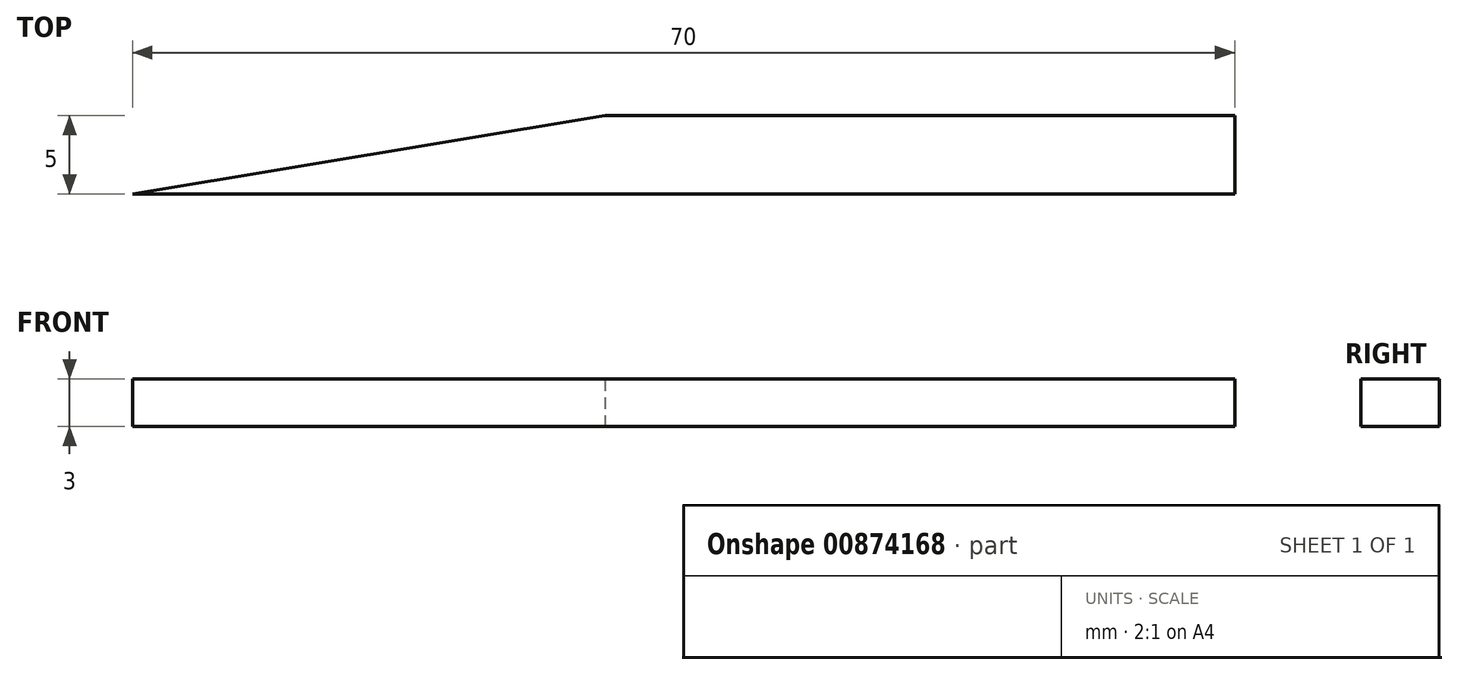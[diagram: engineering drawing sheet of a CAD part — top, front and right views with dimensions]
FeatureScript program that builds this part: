
annotation { "Feature Type Name" : "Feature", "Feature Type Description" : "" }
export const myFeature = defineFeature(function(context is Context, id is Id, definition is map)
    precondition{}
    {
        {
            var Q0;
            Q0=qCreatedBy(makeId("Top.planeOp"),FACE);
            var sketch = newSketch(context, id + "F0", { "sketchPlane" : qUnion([Q0])});
            skLineSegment(sketch, "E0", {"start": v(0, 0) * mm, "end": v(-70, 0) * mm});
            skLineSegment(sketch, "E1", {"start": v(-70, 0) * mm, "end": v(-40, 5) * mm});
            skLineSegment(sketch, "E2", {"start": v(-40, 5) * mm, "end": v(0, 5) * mm});
            skLineSegment(sketch, "E3", {"start": v(0, 5) * mm, "end": v(0, 0) * mm});
            skSolve(sketch);
        }
        {
            var Q0;
            Q0=makeQuery(id+"F0.imprint","IMPRINT",FACE,{"disambiguationData":[TD([[makeQuery(id+"F0.imprint","IMPRINT",EDGE,{"derivedFrom":sQuery(id+"F0.wireOp",EDGE,"E0")}),-1.0]])]});
            extrude(context, id + "F1", {"entities" : qUnion([Q0]), "depth" : 3 * mm, "offsetDistance" : 25.4 * mm});
        }
    });
